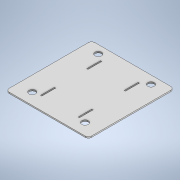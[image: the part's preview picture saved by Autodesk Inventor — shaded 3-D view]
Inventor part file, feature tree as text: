
AUTODESK INVENTOR PART (.ipt)
format: ipt  version: 2022 (Build 260153000, 153)  size: 164,864 bytes
history: native  units: mm
features: extrude x2, sketch x2, fillet x1, projected_geometry x1
ambient origin geometry x8: Origin, YZ Plane, XZ Plane, XY Plane, X Axis, Y Axis, Z Axis, Center Point
bodies: Solid1 (feature_tree)
feature tree (6):
  extrude  "Extrusion1"  Depth=125.0mm
  extrude  "Extrusion2"  Depth=10.0mm
  fillet  "Fillet1"  Radius=100.0mm
  sketch  "Sketch1"  dims[d0=130.0mm d1=125.0mm]
  sketch  "Sketch2"  dims[d2=10.0mm d3=10.0mm d4=100.0mm d5=10.0mm d6=10.0mm d7=100.0mm d8=80.0mm d9=80.0mm d10=17.5mm d11=22.5mm d12=17.5mm d13=22.5mm d14=2.0mm d15=0.0mm d16=55.0mm d17=100.0mm d18=125.0mm d19=35.0mm d20=2.0mm d21=2.0mm d22=2.0mm d23=2.0mm d24=21.0mm d25=21.0mm d26=21.0mm d27=21.0mm d28=19.5mm d29=19.5mm d30=19.5mm d31=19.5mm d32=0.0mm d33=0.0mm d34=5.0mm]
  projected_geometry  "Projected Loop1"
